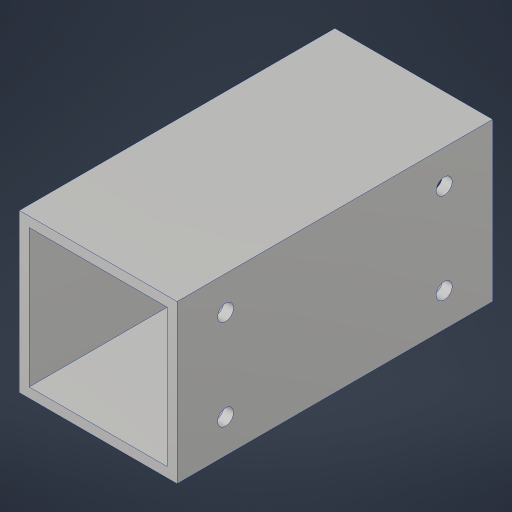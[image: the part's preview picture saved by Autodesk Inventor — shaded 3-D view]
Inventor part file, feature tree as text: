
AUTODESK INVENTOR PART (.ipt)
format: ipt  version: 2023.4 (Build 274418000, 418)  size: 169,472 bytes
history: native  units: in
note: dims shown in document units (in); Inventor stores cm internally (conversion verified against a paired STEP export)
features: extrude x1, hole x1, sketch x1, projected_geometry x1
ambient origin geometry x8: Origin, YZ Plane, XZ Plane, XY Plane, X Axis, Y Axis, Z Axis, Center Point
bodies: Solid1 (feature_tree)
feature tree (4):
  extrude  "Extrusion1"  Depth=3.0in
  hole  "Hole1"  [1 undecoded]
  sketch  "Sketch2"  dims[d4=0.0in d5=3.0in d6=3.1496in d8=360.0deg d10=0.201in d11=0.75in d12=0.385in d13=0.25in d14=0.5635in d15=1.0in d16=0.8108in]
  projected_geometry  "Project Cut Edges1"
note: 1 required parameter value undecoded (feature->parameter linkage not recoverable at this tier; creation-order binding heuristic only, values carry confidence <= 0.55)
